# Revit family: 635-00-001 DN200-250
name_source: partatom
category: Pipe Accessories
units: mm (PartAtom-declared; Revit-internal decimal feet)

## family parameters
Always vertical = No
Cut with Voids When Loaded = No
Part Type = Valve - Breaks Into
Round Connector Dimension = Use Diameter
Shared = No
Work Plane-Based = No

## types (4) — shared parameters
1 = 1 mm  [stored 0.00328084 ft]
10 = 10 mm  [stored 0.0328084 ft]
12 = 11 mm  [stored 0.0360892 ft]
2 = 2 mm  [stored 0.00656168 ft]
4 = 4 mm  [stored 0.0131234 ft]
7 = 7 mm  [stored 0.0229659 ft]
DN0200_PN16_OD_200 = 635-227-00-166
DN0200_PN16_OD_225 = 635-228-00-166
DN0225_PN16_OD_250 = 635-257-00-166
DN0250_PN16_OD_250 = 635-301-00-166
Description_ = AVK SUPA MAXI™ TRANSITION COUPLING, PE100/PN16
Search_table = 635-00-001 DN200-250
URL product pages = https://www.avkvalves.com
zero-valued in all types: Default Elevation

## per-type parameters (varying)
- DN0200_PN16_OD_200: Bolt_End_dis=97 mm  [stored 0.318241 ft]; Bore=100 mm  [stored 0.328084 ft]; Cap_Radius=24 mm  [stored 0.0787402 ft]; D=195 mm; D1=165.75 mm; D11=185.25 mm; D12=175.25 mm; D2=106.15 mm  [stored 0.348261 ft]; D3=58.5 mm  [stored 0.191929 ft]; DN=200 mm; FL_T=67 mm  [stored 0.219816 ft]; FL_T2=33.5 mm; FLange_T1=106.7 mm  [stored 0.350066 ft]; L=648 mm; L1=288 mm; L3=194.4 mm; L4=213.84 mm; L4-L3=13.61 mm; L5=267.3 mm; OD=100 mm  [stored 0.328084 ft]; PCD=155.75 mm; Ring_Dia=122.5 mm; Ring_Dia1=114.54 mm; Ring_dia2=107.27 mm; Ring_dia3=118 mm; Ring_dis=280 mm; SR1=96.5 mm  [stored 0.316601 ft]; SR2=113.5 mm  [stored 0.372375 ft]; Thickness=20 mm  [stored 0.0656168 ft]
- DN0200_PN16_OD_225: Bolt_End_dis=97 mm  [stored 0.318241 ft]; Bore=100.05 mm  [stored 0.328248 ft]; Cap_Radius=24 mm  [stored 0.0787402 ft]; D=195 mm; D1=165.75 mm; D11=185.25 mm; D12=175.25 mm; D2=106.15 mm  [stored 0.348261 ft]; D3=58.5 mm  [stored 0.191929 ft]; DN=200.1 mm; FL_T=67 mm  [stored 0.219816 ft]; FL_T2=33.5 mm; FLange_T1=106.7 mm  [stored 0.350066 ft]; L=648 mm; L1=288 mm; L3=194.4 mm; L4=213.84 mm; L4-L3=13.61 mm; L5=267.3 mm; OD=112.5 mm  [stored 0.369094 ft]; PCD=155.75 mm; Ring_Dia=122.5 mm; Ring_Dia1=114.54 mm; Ring_dia2=113.52 mm; Ring_dia3=124.87 mm; Ring_dis=280 mm; SR1=96.5 mm  [stored 0.316601 ft]; SR2=113.5 mm  [stored 0.372375 ft]; Thickness=22.5 mm  [stored 0.0738189 ft]
- DN0225_PN16_OD_250: Bolt_End_dis=93 mm  [stored 0.305118 ft]; Bore=112.5 mm  [stored 0.369094 ft]; Cap_Radius=30 mm  [stored 0.0984252 ft]; D=218.5 mm; D1=185.73 mm; D11=207.58 mm; D12=197.58 mm; D2=123.2 mm; D3=65.55 mm  [stored 0.215059 ft]; DN=225 mm; FL_T=70 mm  [stored 0.229659 ft]; FL_T2=35 mm  [stored 0.114829 ft]; FLange_T1=102.3 mm  [stored 0.33563 ft]; L=788 mm; L1=353 mm; L3=236.4 mm; L4=260.04 mm; L4-L3=16.55 mm; L5=325.05 mm; OD=125 mm; PCD=175.73 mm; Ring_Dia=148 mm; Ring_Dia1=138.38 mm; Ring_dia2=131.69 mm; Ring_dia3=144.86 mm; Ring_dis=380 mm; SR1=112 mm  [stored 0.367454 ft]; SR2=128.5 mm; Thickness=25 mm  [stored 0.082021 ft]
- DN0250_PN16_OD_250: Bolt_End_dis=103 mm  [stored 0.337927 ft]; Bore=125 mm; Cap_Radius=33 mm  [stored 0.108268 ft]; D=242.5 mm; D1=206.13 mm; D11=230.38 mm; D12=220.38 mm; D2=146.3 mm; D3=72.75 mm  [stored 0.238681 ft]; DN=250 mm; FL_T=70 mm  [stored 0.229659 ft]; FL_T2=35 mm  [stored 0.114829 ft]; FLange_T1=113.3 mm  [stored 0.371719 ft]; L=784 mm; L1=353 mm; L3=235.2 mm; L4=258.72 mm; L4-L3=16.46 mm; L5=323.4 mm; OD=125 mm; PCD=196.13 mm; Ring_Dia=148 mm; Ring_Dia1=138.38 mm; Ring_dia2=131.69 mm; Ring_dia3=144.86 mm; Ring_dis=385 mm; SR1=133 mm; SR2=150.5 mm; Thickness=25 mm  [stored 0.082021 ft]

note: [stored X ft] marks values corroborated as IEEE doubles in the binary element streams (Revit-internal decimal feet)

## geometry (parser evidence)
native form markers: Sweep x3
no freeform markers — native parametric forms only
